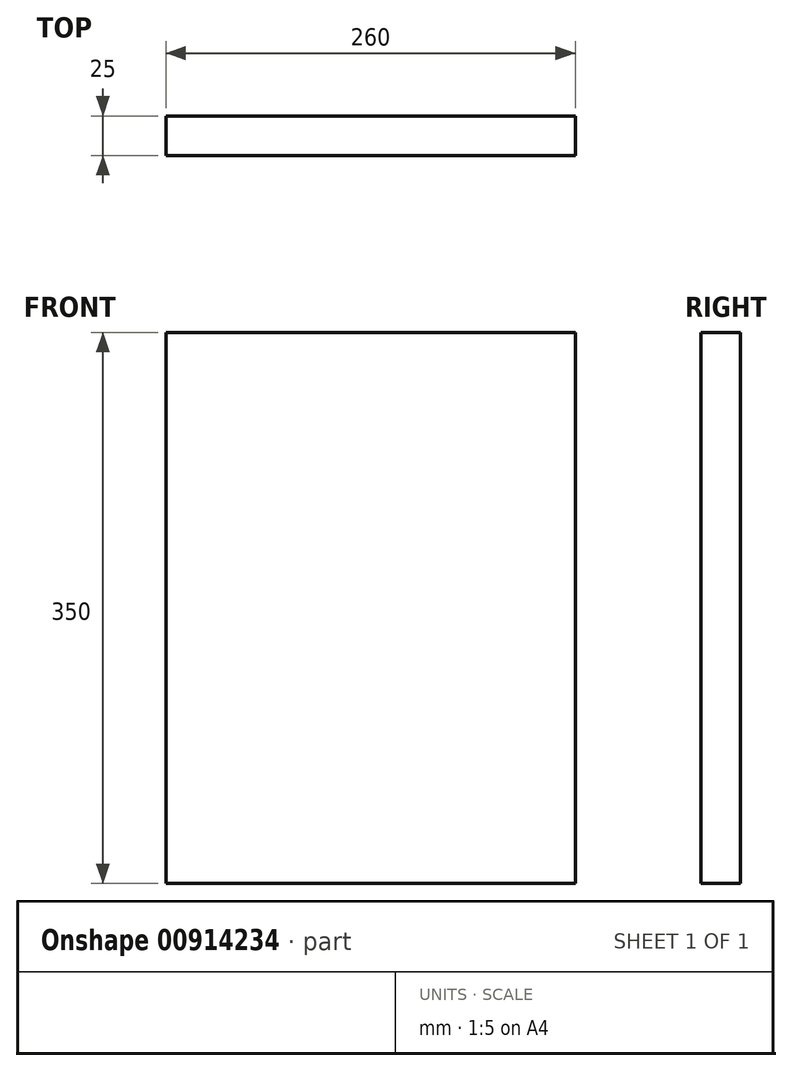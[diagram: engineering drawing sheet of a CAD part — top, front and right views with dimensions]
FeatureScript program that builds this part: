
annotation { "Feature Type Name" : "Feature", "Feature Type Description" : "" }
export const myFeature = defineFeature(function(context is Context, id is Id, definition is map)
    precondition{}
    {
        {
            var Q0;
            Q0=qCreatedBy(makeId("Front.planeOp"),FACE);
            var sketch = newSketch(context, id + "F0", { "sketchPlane" : qUnion([Q0])});
            skLineSegment(sketch, "E0.bottom", {"start": v(-123.24, 182.75) * mm, "end": v(136.76, 182.75) * mm});
            skLineSegment(sketch, "E0.top", {"start": v(-123.24, -167.25) * mm, "end": v(136.76, -167.25) * mm});
            skLineSegment(sketch, "E0.left", {"start": v(-123.24, 182.75) * mm, "end": v(-123.24, -167.25) * mm});
            skLineSegment(sketch, "E0.right", {"start": v(136.76, 182.75) * mm, "end": v(136.76, -167.25) * mm});
            skSolve(sketch);
        }
        {
            var Q0;
            Q0=makeQuery(id+"F0.imprint","IMPRINT",FACE,{"disambiguationData":[TD([[makeQuery(id+"F0.imprint","IMPRINT",EDGE,{"derivedFrom":sQuery(id+"F0.wireOp",EDGE,"E0.bottom")}),-1.0]])]});
            extrude(context, id + "F1", {"entities" : qUnion([Q0]), "depth" : 25 * mm, "offsetDistance" : 25 * mm});
        }
    });
